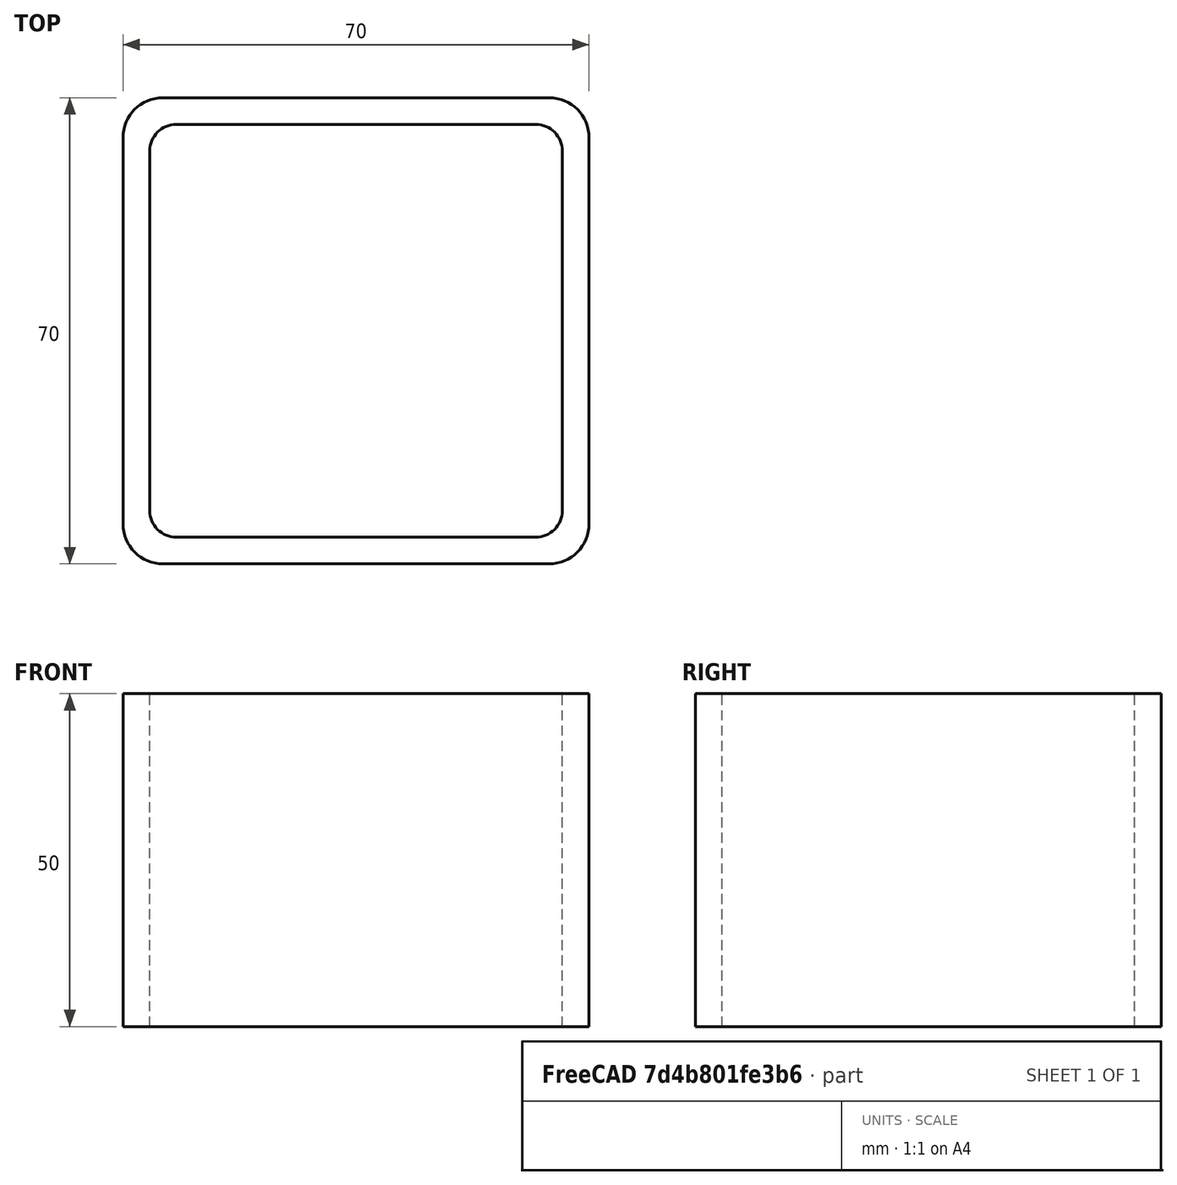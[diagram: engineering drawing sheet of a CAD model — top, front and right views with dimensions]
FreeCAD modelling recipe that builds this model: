
FCSTD DOCUMENT  (FreeCAD 0.15R4671 (Git))
Label: Square hollow section 70x70x4 EN10219 S235JRH
License: All rights reserved
LicenseURL: http://en.wikipedia.org/wiki/All_rights_reserved
objects: Sketcher::SketchObject×1, Part::Extrusion×1
note: 2 computed .brp shape members not serialized (recipe doc carries the construction recipe); baked Part::Feature solids carry a one-line shape summary decoded from their .brp

FEATURE [Sketcher::SketchObject] Sketch
  sketch-geometry (16):
    g0: LineSegment StartX=-27 StartY=31 StartZ=0 EndX=27 EndY=31 EndZ=0
    g1: LineSegment StartX=31 StartY=27 StartZ=0 EndX=31 EndY=-27 EndZ=0
    g2: LineSegment StartX=27 StartY=-31 StartZ=0 EndX=-27 EndY=-31 EndZ=0
    g3: LineSegment StartX=-31 StartY=-27 StartZ=0 EndX=-31 EndY=27 EndZ=0
    g4: LineSegment StartX=-29 StartY=35 StartZ=0 EndX=29 EndY=35 EndZ=0
    g5: LineSegment StartX=35 StartY=29 StartZ=0 EndX=35 EndY=-29 EndZ=0
    g6: LineSegment StartX=29 StartY=-35 StartZ=0 EndX=-29 EndY=-35 EndZ=0
    g7: LineSegment StartX=-35 StartY=-29 StartZ=0 EndX=-35 EndY=29 EndZ=0
    g8: ArcOfCircle CenterX=-27 CenterY=27 CenterZ=0 NormalX=0 NormalY=0 NormalZ=1 Radius=4 StartAngle=1.5708 EndAngle=3.14159
    g9: ArcOfCircle CenterX=27 CenterY=27 CenterZ=0 NormalX=0 NormalY=0 NormalZ=1 Radius=4 StartAngle=0 EndAngle=1.5708
    g10: ArcOfCircle CenterX=27 CenterY=-27 CenterZ=0 NormalX=0 NormalY=0 NormalZ=1 Radius=4 StartAngle=4.71239 EndAngle=6.28319
    g11: ArcOfCircle CenterX=-27 CenterY=-27 CenterZ=0 NormalX=0 NormalY=0 NormalZ=1 Radius=4 StartAngle=3.14159 EndAngle=4.71239
    g12: ArcOfCircle CenterX=29 CenterY=29 CenterZ=0 NormalX=0 NormalY=0 NormalZ=1 Radius=6 StartAngle=0 EndAngle=1.5708
    g13: ArcOfCircle CenterX=29 CenterY=-29 CenterZ=0 NormalX=0 NormalY=0 NormalZ=1 Radius=6 StartAngle=4.71239 EndAngle=6.28319
    g14: ArcOfCircle CenterX=-29 CenterY=-29 CenterZ=0 NormalX=0 NormalY=0 NormalZ=1 Radius=6 StartAngle=3.14159 EndAngle=4.71239
    g15: ArcOfCircle CenterX=-29 CenterY=29 CenterZ=0 NormalX=0 NormalY=0 NormalZ=1 Radius=6 StartAngle=1.5708 EndAngle=3.14159
  constraints (36):
    c: Horizontal(g2)
    c: Vertical(g3)
    c: Horizontal(g6)
    c: Vertical(g7)
    c: Tangent(g3,g8) = 1.5708
    c: Tangent(g0,g8) = 1.5708
    c: Tangent(g0,g9) = 1.5708
    c: Tangent(g1,g9) = 1.5708
    c: Tangent(g1,g10) = 1.5708
    c: Tangent(g2,g10) = 1.5708
    c: Tangent(g2,g11) = 1.5708
    c: Tangent(g3,g11) = 1.5708
    c: Tangent(g4,g12) = 1.5708
    c: Tangent(g5,g12) = 1.5708
    c: Tangent(g5,g13) = 1.5708
    c: Tangent(g6,g13) = 1.5708
    c: Tangent(g6,g14) = 1.5708
    c: Tangent(g7,g14) = 1.5708
    c: Tangent(g7,g15) = 1.5708
    c: Tangent(g4,g15) = 1.5708
    c: Equal(g9,g8)
    c: Equal(g9,g11)
    c: Equal(g9,g10)
    c: Equal(g12,g15)
    c: Equal(g12,g14)
    c: Equal(g12,g13)
    c: Symmetric(g4,g6,g-1)
    c: Symmetric(g7,g5,g-2)
    c: DistanceY(g4,g6) = -70
    c: DistanceX(g7,g5) = 70
    c: Symmetric(g3,g1,g-2)
    c: Symmetric(g0,g2,g-1)
    c: DistanceY(g0,g4) = 4
    c: DistanceX(g5,g1) = -4
    c: Radius(g9) = 4
    c: Radius(g12) = 6
FEATURE [Part::Extrusion] Extrude  label="Square hollow section 70x70x4 EN10219 S235JRH"
  Base = -> Sketch
  Dir = (0,0,50)
  Solid = true
